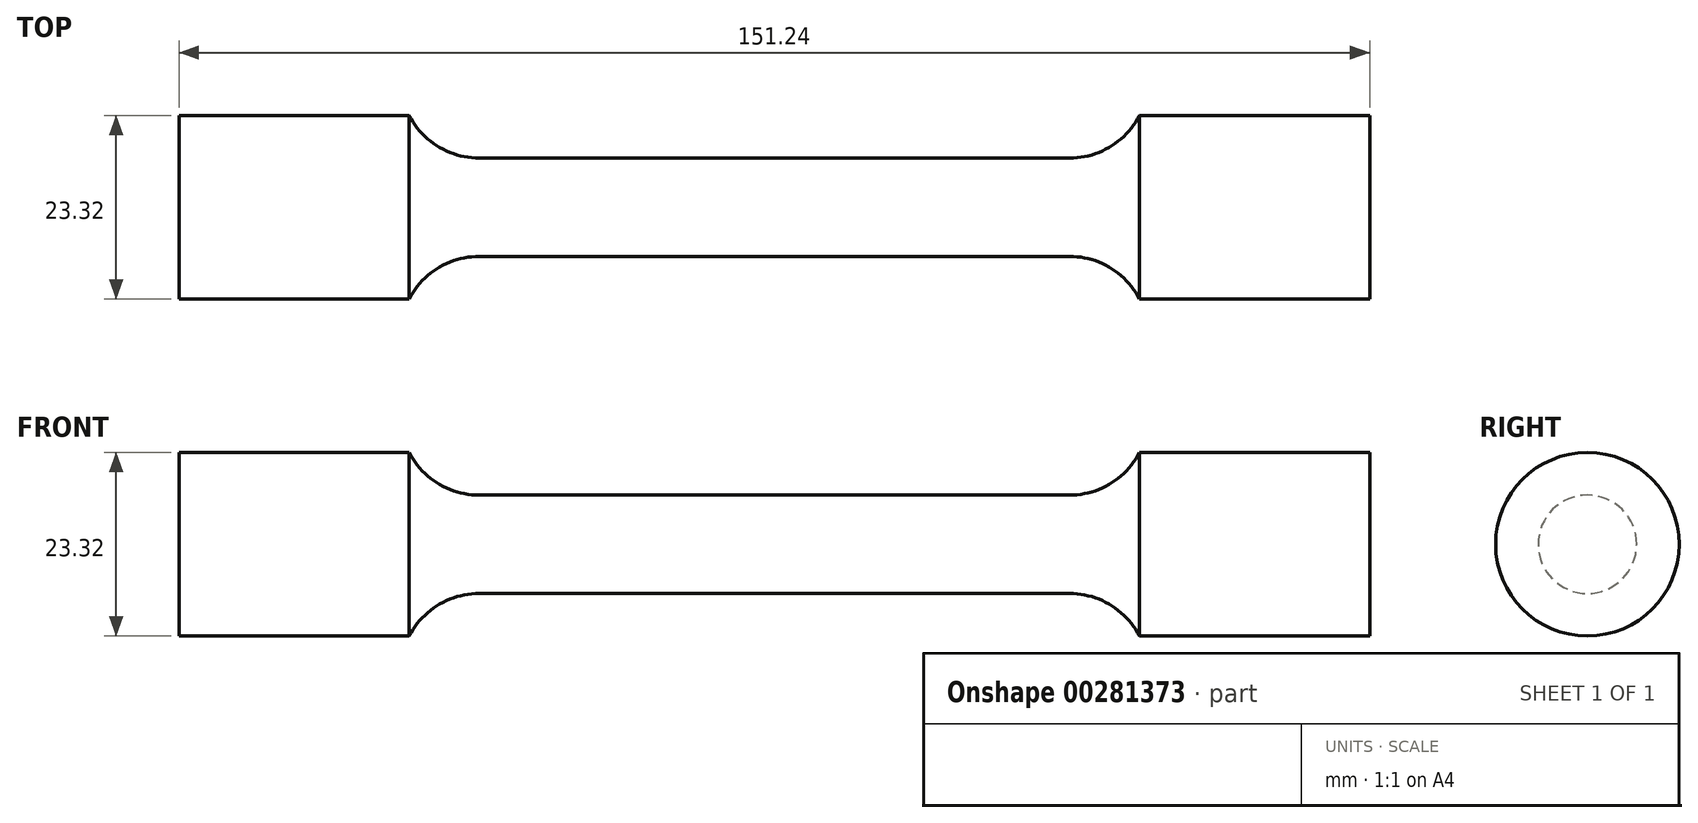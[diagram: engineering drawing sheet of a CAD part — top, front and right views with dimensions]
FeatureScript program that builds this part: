
annotation { "Feature Type Name" : "Feature", "Feature Type Description" : "" }
export const myFeature = defineFeature(function(context is Context, id is Id, definition is map)
    precondition{}
    {
        {
            var Q0;
            Q0=qCreatedBy(makeId("Front.planeOp"),FACE);
            var sketch = newSketch(context, id + "F0", { "sketchPlane" : qUnion([Q0])});
            skLineSegment(sketch, "E0", {"start": v(0, 6.25) * mm, "end": v(37.5, 6.25) * mm});
            skArc(sketch, "E1", {"start": v(37.5, 6.25) * mm, "mid": v(42.7, 7.7) * mm, "end": v(46.38, 11.66) * mm});
            skLineSegment(sketch, "E2", {"start": v(46.38, 11.66) * mm, "end": v(75.62, 11.66) * mm});
            skLineSegment(sketch, "E3", {"start": v(75.62, 11.66) * mm, "end": v(75.62, 0) * mm});
            skLineSegment(sketch, "E4", {"start": v(75.62, 0) * mm, "end": v(0, 0) * mm});
            skArc(sketch, "E5.MirrorCS", {"start": v(-37.5, 6.25) * mm, "mid": v(-42.7, 7.7) * mm, "end": v(-46.38, 11.66) * mm});
            skLineSegment(sketch, "E6.MirrorCS", {"start": v(-46.38, 11.66) * mm, "end": v(-75.62, 11.66) * mm});
            skLineSegment(sketch, "E7.MirrorCS", {"start": v(-75.62, 0) * mm, "end": v(0, 0) * mm});
            skLineSegment(sketch, "E8.MirrorCS", {"start": v(-75.62, 11.66) * mm, "end": v(-75.62, 0) * mm});
            skLineSegment(sketch, "E9.MirrorCS", {"start": v(0, 6.25) * mm, "end": v(-37.5, 6.25) * mm});
            skSolve(sketch);
        }
        {
            var Q0;
            Q0=makeQuery(id+"F0.imprint","IMPRINT",FACE,{"disambiguationData":[TD([[makeQuery(id+"F0.imprint","IMPRINT",EDGE,{"derivedFrom":sQuery(id+"F0.wireOp",EDGE,"E0")}),-1.0]])]});
            var Q1;
            Q1=sQuery(id+"F0.wireOp",EDGE,"E4");
            revolve(context, id + "F1", {"entities" : qUnion([Q0]), "axis" : qUnion([Q1]), "revolveType" : RevolveType.FULL});
        }
    });
